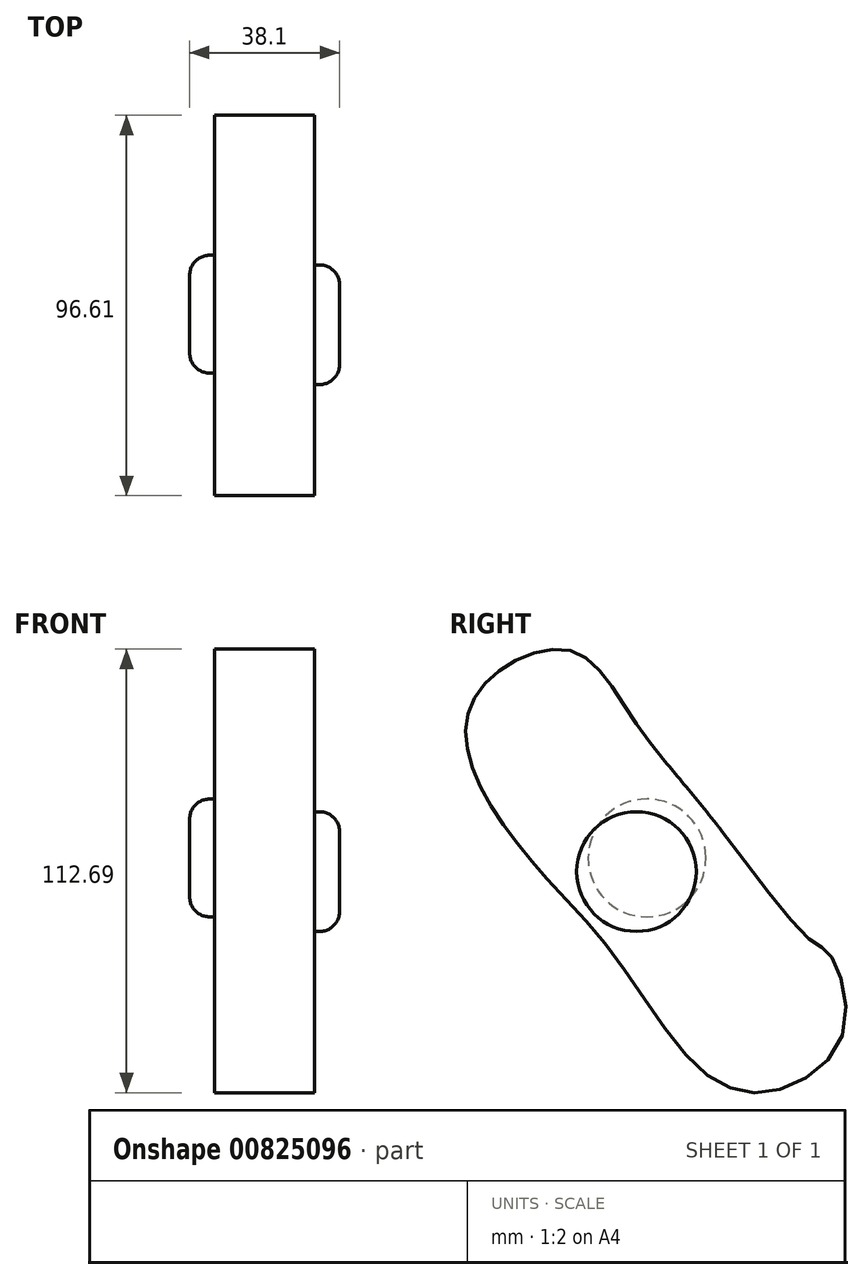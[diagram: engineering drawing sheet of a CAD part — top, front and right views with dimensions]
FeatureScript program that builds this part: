
annotation { "Feature Type Name" : "Feature", "Feature Type Description" : "" }
export const myFeature = defineFeature(function(context is Context, id is Id, definition is map)
    precondition{}
    {
        {
            var Q0;
            Q0=qCreatedBy(makeId("Right.planeOp"),FACE);
            var sketch = newSketch(context, id + "F0", { "sketchPlane" : qUnion([Q0])});
            skFitSpline(sketch, "E0", {"points": [v(41.42, -20.8) * mm, v(17.7, 8.53) * mm, v(-3.87, 35.7) * mm, v(-17.67, 52.1) * mm, v(-35.36, 49.08) * mm, v(-45.71, 35.7) * mm, v(-41.83, 17.16) * mm, v(-25.44, -5.27) * mm, v(-7.75, -25.55) * mm, v(13.82, -54.02) * mm, v(31.93, -59.2) * mm, v(49.62, -44.96) * mm, v(46.6, -24.68) * mm, v(41.42, -20.8) * mm]});
            skFitSpline(sketch, "E1", {"points": [v(4.58, 24.54) * mm, v(-14.22, 20.6) * mm, v(-21.56, 8.1) * mm, v(-25.44, 0) * mm, v(-25.44, -5.27) * mm], "startDerivative": vector(-66.72, -2.28) * mm, "endDerivative": vector(4, -30.53) * mm});
            skFitSpline(sketch, "E2", {"points": [v(20.45, -5.88) * mm, v(17.7, -13.58) * mm, v(6.34, -21.78) * mm, v(-5.97, -20.24) * mm, v(-13.66, -13.06) * mm, v(-16.74, -2.8) * mm, v(-11.35, 8.53) * mm, v(-2.38, 15.66) * mm, v(11.22, 12.84) * mm, v(18.68, 7.28) * mm, v(21.73, -2.03) * mm, v(20.45, -5.88) * mm]});
            skSolve(sketch);
        }
        {
            var Q0;
            {var subQ0=sQuery(id+"F0.wireOp",EDGE,"E1");Q0=makeQuery(id+"F0.imprint","IMPRINT",FACE,{"disambiguationData":[TD([[makeQuery(id+"F0.imprint","IMPRINT",EDGE,{"derivedFrom":subQ0}),1.0]])]});}
            var Q1;
            {var subQ0=sQuery(id+"F0.wireOp",EDGE,"E1");Q1=makeQuery(id+"F0.imprint","IMPRINT",FACE,{"disambiguationData":[TD([[makeQuery(id+"F0.imprint","IMPRINT",EDGE,{"derivedFrom":subQ0}),-1.0]])]});}
            var Q2;
            {var subQ0=sQuery(id+"F0.wireOp",EDGE,"E2");var subQ1=sQuery(id+"F0.wireOp",EDGE,"E0");var subQ2=makeQuery(id+"F0.imprint","INTERSECT",VERTEX,{"disambiguationData":[OD(0.0)],"derivedFrom":[subQ1,subQ0]});Q2=makeQuery(id+"F0.imprint","IMPRINT",FACE,{"disambiguationData":[TD([[makeQuery(id+"F0.imprint","IMPRINT",EDGE,{"disambiguationData":[TD([[subQ2,1.0]])],"derivedFrom":subQ1}),1.0]])]});}
            extrude(context, id + "F1", {"entities" : qUnion([Q0, Q1, Q2]), "depth" : 25.4 * mm, "offsetDistance" : 25.4 * mm});
        }
        {
            var Q0;
            Q0=makeQuery(id+"F1.opExtrude","CAP_FACE",FACE,{"disambiguationData":[OSD([sQuery(id+"F0.wireOp",EDGE,"E0")])],"isStart":false});
            var sketch = newSketch(context, id + "F2", { "sketchPlane" : qUnion([Q0])});
            skCircle(sketch, "E3", {"center": v(-2.68, -3.47) * mm, "radius": 15.2 * mm});
            skSolve(sketch);
        }
        {
            var Q0;
            Q0 = qSketchRegion(id + "F2", true);
            extrude(context, id + "F3", {"entities" : qUnion([Q0]), "operationType" : NewBodyOperationType.ADD, "depth" : 6.35 * mm, "offsetDistance" : 25.4 * mm});
        }
        {
            var Q0;
            Q0=makeQuery(id+"F3.opExtrude","CAP_EDGE",EDGE,{"disambiguationData":[OSD([sQuery(id+"F2.wireOp",EDGE,"E3")])],"isStart":false});
            fillet(context, id + "F4", {"entities" : qUnion([Q0]), "radius" : 5.08 * mm, "tangentPropagation" : true, "allowEdgeOverflow" : false});
        }
        {
            var Q0;
            Q0=makeQuery(id+"F1.opExtrude","CAP_FACE",FACE,{"disambiguationData":[OSD([sQuery(id+"F0.wireOp",EDGE,"E0")])],"isStart":true});
            var sketch = newSketch(context, id + "F5", { "sketchPlane" : qUnion([Q0])});
            skCircle(sketch, "E4", {"center": v(0, 0) * mm, "radius": 14.97 * mm});
            skSolve(sketch);
        }
        {
            var Q0;
            Q0=makeQuery(id+"F5.imprint","IMPRINT",FACE,{"disambiguationData":[TD([[makeQuery(id+"F5.imprint","IMPRINT",EDGE,{"derivedFrom":sQuery(id+"F5.wireOp",EDGE,"E4")}),1.0]])]});
            extrude(context, id + "F6", {"entities" : qUnion([Q0]), "operationType" : NewBodyOperationType.ADD, "depth" : 6.35 * mm, "offsetDistance" : 25.4 * mm});
        }
        {
            var Q0;
            Q0=makeQuery(id+"F6.opExtrude","CAP_FACE",FACE,{"disambiguationData":[OSD([sQuery(id+"F5.wireOp",EDGE,"E4")])],"isStart":false});
            fillet(context, id + "F7", {"entities" : qUnion([Q0]), "radius" : 5.08 * mm, "tangentPropagation" : true, "allowEdgeOverflow" : false});
        }
    });
